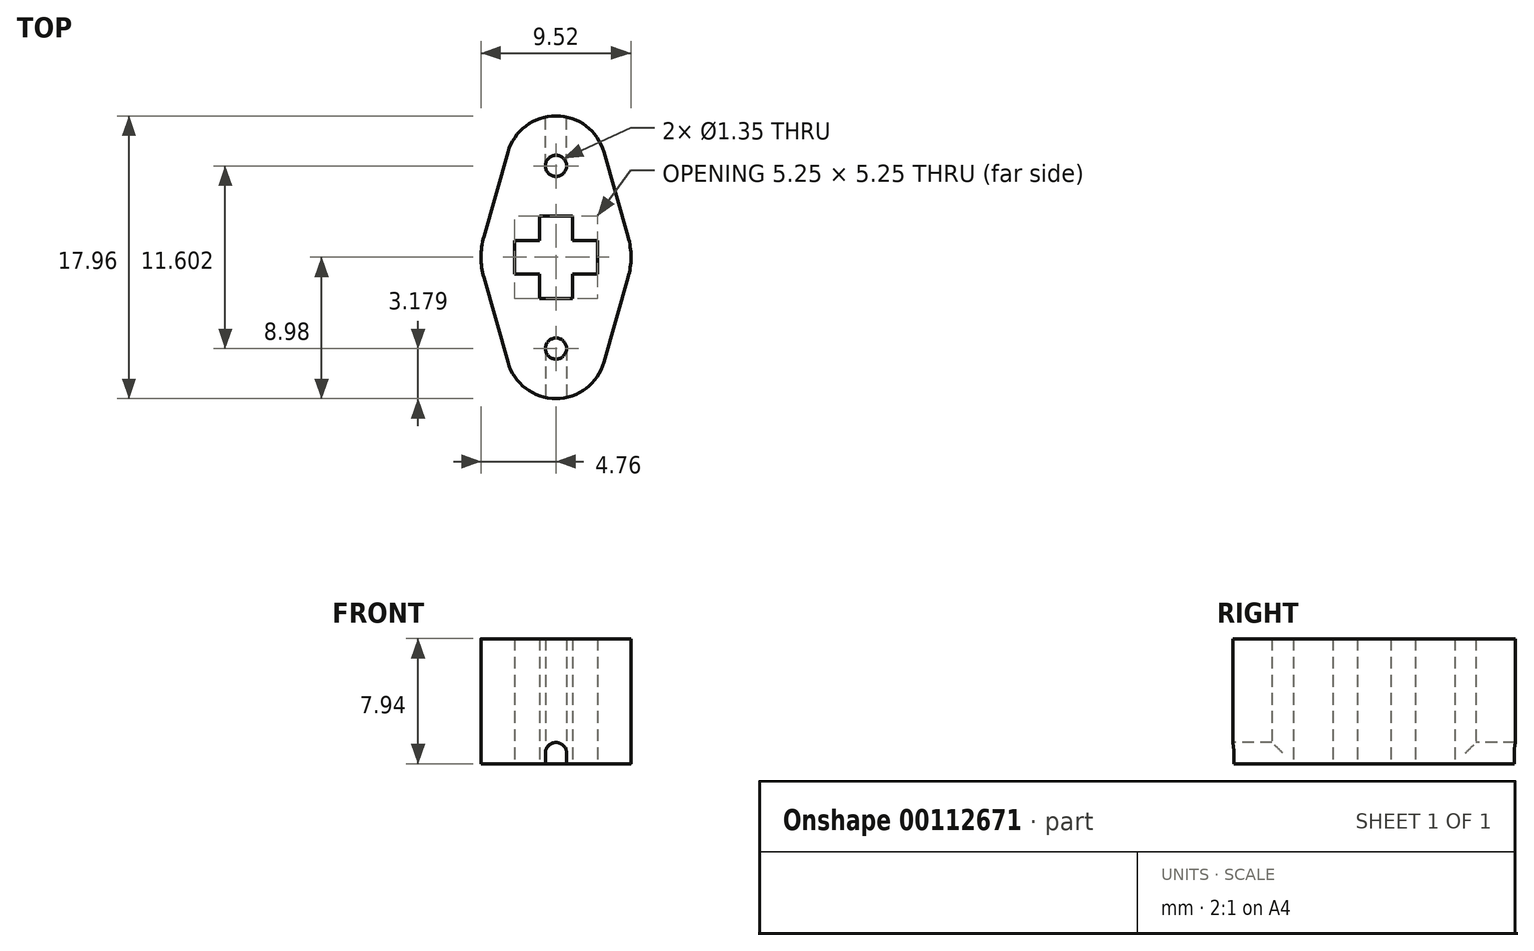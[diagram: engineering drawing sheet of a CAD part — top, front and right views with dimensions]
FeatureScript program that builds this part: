
annotation { "Feature Type Name" : "Feature", "Feature Type Description" : "" }
export const myFeature = defineFeature(function(context is Context, id is Id, definition is map)
    precondition{}
    {
        {
            var Q0;
            Q0=qCreatedBy(makeId("Top.planeOp"),FACE);
            var sketch = newSketch(context, id + "F0", { "sketchPlane" : qUnion([Q0])});
            skLineSegment(sketch, "E0.bottom", {"start": v(1.06, 2.63) * mm, "end": v(-1.06, 2.63) * mm});
            skLineSegment(sketch, "E0.top", {"start": v(1.06, -2.63) * mm, "end": v(-1.06, -2.63) * mm});
            skLineSegment(sketch, "E0.left", {"start": v(1.06, 2.63) * mm, "end": v(1.06, -2.63) * mm});
            skLineSegment(sketch, "E0.right", {"start": v(-1.06, 2.63) * mm, "end": v(-1.06, -2.63) * mm});
            skPoint(sketch, "E0.middle", {"position": v(0, 0) * mm});
            skLineSegment(sketch, "E1.bottom", {"start": v(2.63, -1.06) * mm, "end": v(-2.63, -1.06) * mm});
            skLineSegment(sketch, "E1.top", {"start": v(2.63, 1.06) * mm, "end": v(-2.63, 1.06) * mm});
            skLineSegment(sketch, "E1.left", {"start": v(2.63, -1.06) * mm, "end": v(2.63, 1.06) * mm});
            skLineSegment(sketch, "E1.right", {"start": v(-2.63, -1.06) * mm, "end": v(-2.63, 1.06) * mm});
            skLineSegment(sketch, "E2", {"start": v(-4.58, -1.3) * mm, "end": v(-3.05, -6.67) * mm});
            skLineSegment(sketch, "E3", {"start": v(4.58, -1.3) * mm, "end": v(3.05, -6.67) * mm});
            skLineSegment(sketch, "E4", {"start": v(0, 0) * mm, "end": v(0, -5.8) * mm, "construction": true});
            skArc(sketch, "E5", {"start": v(-3.05, -6.67) * mm, "mid": v(0, -8.98) * mm, "end": v(3.05, -6.67) * mm});
            skLineSegment(sketch, "E6", {"start": v(0, 0) * mm, "end": v(0, 5.8) * mm, "construction": true});
            skCircle(sketch, "E7", {"center": v(0, 5.8) * mm, "radius": 0.67 * mm});
            skCircle(sketch, "E8", {"center": v(0, -5.8) * mm, "radius": 0.67 * mm});
            skArc(sketch, "E9", {"start": v(3.05, -6.67) * mm, "mid": v(0, -2.63) * mm, "end": v(-3.05, -6.67) * mm, "construction": true});
            skArc(sketch, "E10", {"start": v(-4.58, 1.3) * mm, "mid": v(-4.76, 0) * mm, "end": v(-4.58, -1.3) * mm});
            skArc(sketch, "E11", {"start": v(4.58, -1.3) * mm, "mid": v(4.76, 0) * mm, "end": v(4.58, 1.3) * mm});
            skArc(sketch, "E12", {"start": v(3.05, 6.67) * mm, "mid": v(0, 8.98) * mm, "end": v(-3.05, 6.67) * mm});
            skLineSegment(sketch, "E13", {"start": v(-4.58, 1.3) * mm, "end": v(-3.05, 6.67) * mm});
            skLineSegment(sketch, "E14", {"start": v(4.58, 1.3) * mm, "end": v(3.05, 6.67) * mm});
            skSolve(sketch);
        }
        {
            var Q0;
            Q0=qSketchRegion(id+"F0",true);
            extrude(context, id + "F1", {"entities" : qUnion([Q0]), "depth" : 7.94 * mm});
        }
        {
            var Q0;
            Q0=makeQuery(id+"F1.opExtrude","CAP_FACE",FACE,{"disambiguationData":[OSD([sQuery(id+"F0.wireOp",EDGE,"E0.bottom"),sQuery(id+"F0.wireOp",EDGE,"E0.top"),sQuery(id+"F0.wireOp",EDGE,"E0.left"),sQuery(id+"F0.wireOp",EDGE,"E0.right"),sQuery(id+"F0.wireOp",EDGE,"E1.bottom"),sQuery(id+"F0.wireOp",EDGE,"E1.top"),sQuery(id+"F0.wireOp",EDGE,"E1.left"),sQuery(id+"F0.wireOp",EDGE,"E1.right"),sQuery(id+"F0.wireOp",EDGE,"E2"),sQuery(id+"F0.wireOp",EDGE,"E3"),sQuery(id+"F0.wireOp",EDGE,"E5"),sQuery(id+"F0.wireOp",EDGE,"E7"),sQuery(id+"F0.wireOp",EDGE,"E8"),sQuery(id+"F0.wireOp",EDGE,"E10"),sQuery(id+"F0.wireOp",EDGE,"E11"),sQuery(id+"F0.wireOp",EDGE,"E12"),sQuery(id+"F0.wireOp",EDGE,"E13"),sQuery(id+"F0.wireOp",EDGE,"E14")])],"isStart":true});
            var sketch = newSketch(context, id + "F2", { "sketchPlane" : qUnion([Q0])});
            skLineSegment(sketch, "E15.bottom", {"start": v(0.67, 5.8) * mm, "end": v(-0.67, 5.8) * mm});
            skLineSegment(sketch, "E15.top", {"start": v(0.67, 8.9) * mm, "end": v(-0.67, 8.9) * mm, "construction": true});
            skLineSegment(sketch, "E15.left", {"start": v(0.67, 5.8) * mm, "end": v(0.67, 8.9) * mm});
            skLineSegment(sketch, "E15.right", {"start": v(-0.67, 5.8) * mm, "end": v(-0.67, 8.9) * mm});
            skPoint(sketch, "E16", {"position": v(0, 5.8) * mm});
            skArc(sketch, "E17", {"start": v(0.67, 8.9) * mm, "mid": v(0, 8.98) * mm, "end": v(-0.67, 8.9) * mm});
            skLineSegment(sketch, "E18.bottom", {"start": v(0.67, -5.8) * mm, "end": v(-0.67, -5.8) * mm});
            skLineSegment(sketch, "E18.top", {"start": v(0.67, -8.9) * mm, "end": v(-0.67, -8.9) * mm, "construction": true});
            skLineSegment(sketch, "E18.left", {"start": v(0.67, -5.8) * mm, "end": v(0.67, -8.9) * mm});
            skLineSegment(sketch, "E18.right", {"start": v(-0.67, -5.8) * mm, "end": v(-0.67, -8.9) * mm});
            skArc(sketch, "E19", {"start": v(-0.67, -8.9) * mm, "mid": v(0, -8.98) * mm, "end": v(0.67, -8.9) * mm});
            skSolve(sketch);
        }
        {
            var Q0;
            Q0=qSketchRegion(id+"F2",true);
            extrude(context, id + "F3", {"entities" : qUnion([Q0]), "operationType" : NewBodyOperationType.REMOVE, "oppositeDirection" : true, "depth" : 1.35 * mm});
        }
        {
            var Q0;
            Q0=makeQuery(id+"F3.boolean.opBoolean","COPY",EDGE,{"derivedFrom":makeQuery(id+"F3.opExtrude","CAP_EDGE",EDGE,{"disambiguationData":[OSD([sQuery(id+"F2.wireOp",EDGE,"E18.left")])],"isStart":false})});
            var Q1;
            Q1=makeQuery(id+"F3.boolean.opBoolean","COPY",EDGE,{"derivedFrom":makeQuery(id+"F3.opExtrude","CAP_EDGE",EDGE,{"disambiguationData":[OSD([sQuery(id+"F2.wireOp",EDGE,"E18.right")])],"isStart":false})});
            var Q2;
            Q2=makeQuery(id+"F3.boolean.opBoolean","COPY",EDGE,{"derivedFrom":makeQuery(id+"F3.opExtrude","CAP_EDGE",EDGE,{"disambiguationData":[OSD([sQuery(id+"F2.wireOp",EDGE,"E15.left")])],"isStart":false})});
            var Q3;
            Q3=makeQuery(id+"F3.boolean.opBoolean","COPY",EDGE,{"derivedFrom":makeQuery(id+"F3.opExtrude","CAP_EDGE",EDGE,{"disambiguationData":[OSD([sQuery(id+"F2.wireOp",EDGE,"E15.right")])],"isStart":false})});
            fillet(context, id + "F4", {"entities" : qUnion([Q0, Q1, Q2, Q3]), "radius" : 0.67 * mm, "tangentPropagation" : true, "allowEdgeOverflow" : false});
        }
    });
